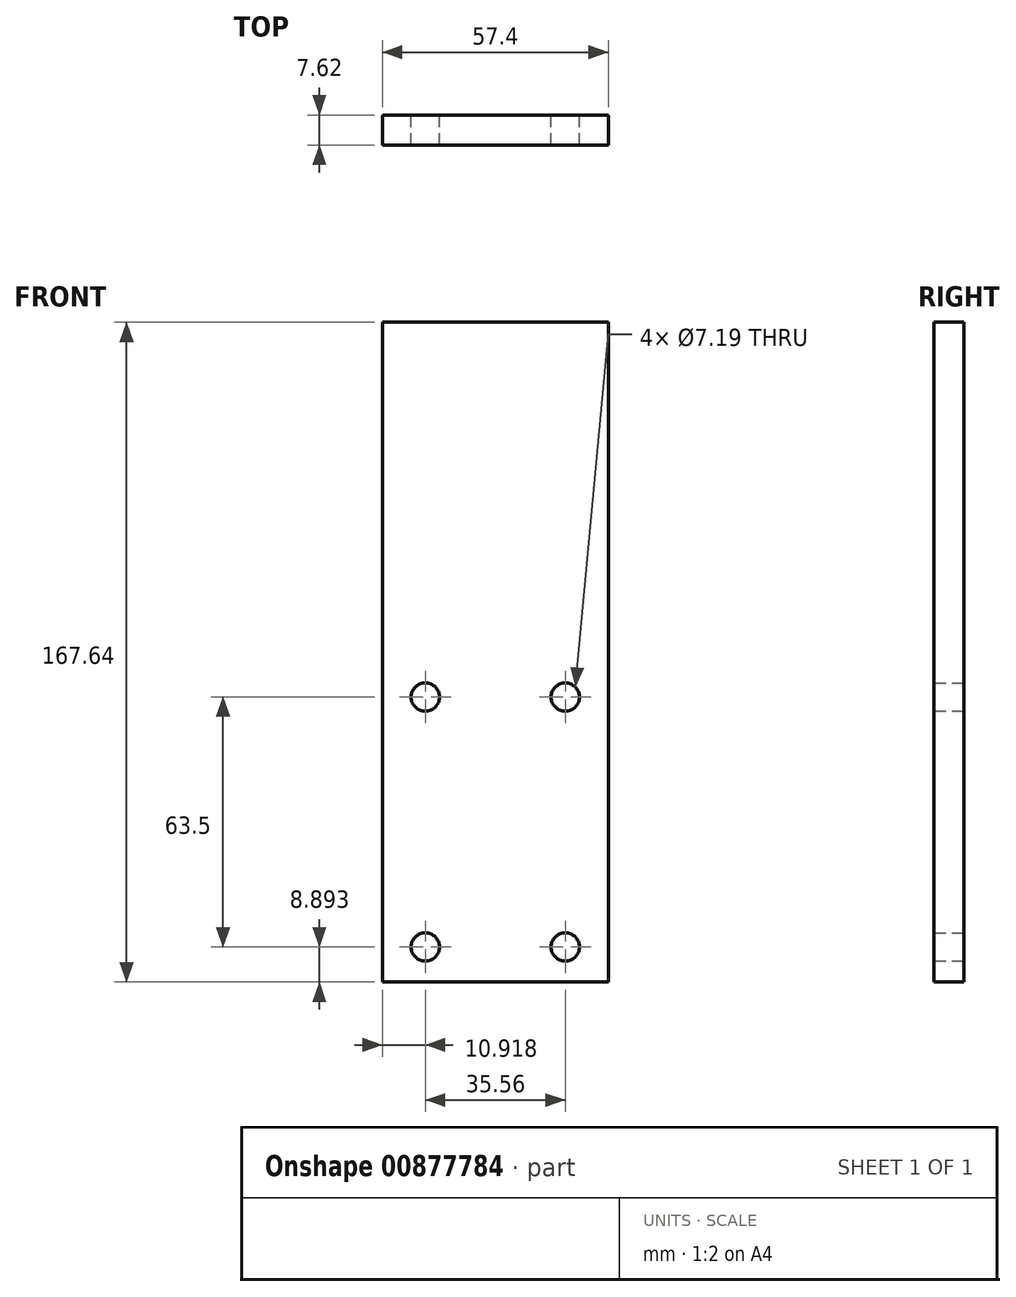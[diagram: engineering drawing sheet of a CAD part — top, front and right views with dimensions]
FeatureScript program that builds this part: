
annotation { "Feature Type Name" : "Feature", "Feature Type Description" : "" }
export const myFeature = defineFeature(function(context is Context, id is Id, definition is map)
    precondition{}
    {
        {
            var Q0;
            Q0=qCreatedBy(makeId("Front.planeOp"),FACE);
            var sketch = newSketch(context, id + "F0", { "sketchPlane" : qUnion([Q0])});
            skCircle(sketch, "E0", {"center": v(-45.4, -33.32) * mm, "radius": 3.6 * mm});
            skCircle(sketch, "E1", {"center": v(-9.83, -33.32) * mm, "radius": 3.6 * mm});
            skCircle(sketch, "E2", {"center": v(-45.4, 30.18) * mm, "radius": 3.6 * mm});
            skCircle(sketch, "E3", {"center": v(-9.83, 30.18) * mm, "radius": 3.6 * mm});
            skLineSegment(sketch, "E4", {"start": v(-56.31, -42.2) * mm, "end": v(1.1, -42.2) * mm});
            skLineSegment(sketch, "E5", {"start": v(-56.31, -42.2) * mm, "end": v(-56.31, 125.43) * mm});
            skLineSegment(sketch, "E6", {"start": v(1.1, -42.2) * mm, "end": v(1.1, 125.43) * mm});
            skLineSegment(sketch, "E7", {"start": v(-56.31, 125.43) * mm, "end": v(1.1, 125.43) * mm});
            skSolve(sketch);
        }
        {
            var Q0;
            Q0=makeQuery(id+"F0.imprint","IMPRINT",FACE,{"disambiguationData":[TD([[makeQuery(id+"F0.imprint","IMPRINT",EDGE,{"derivedFrom":sQuery(id+"F0.wireOp",EDGE,"E0")}),-1.0]])]});
            extrude(context, id + "F1", {"entities" : qUnion([Q0]), "depth" : 7.62 * mm, "offsetDistance" : 25.4 * mm});
        }
    });
